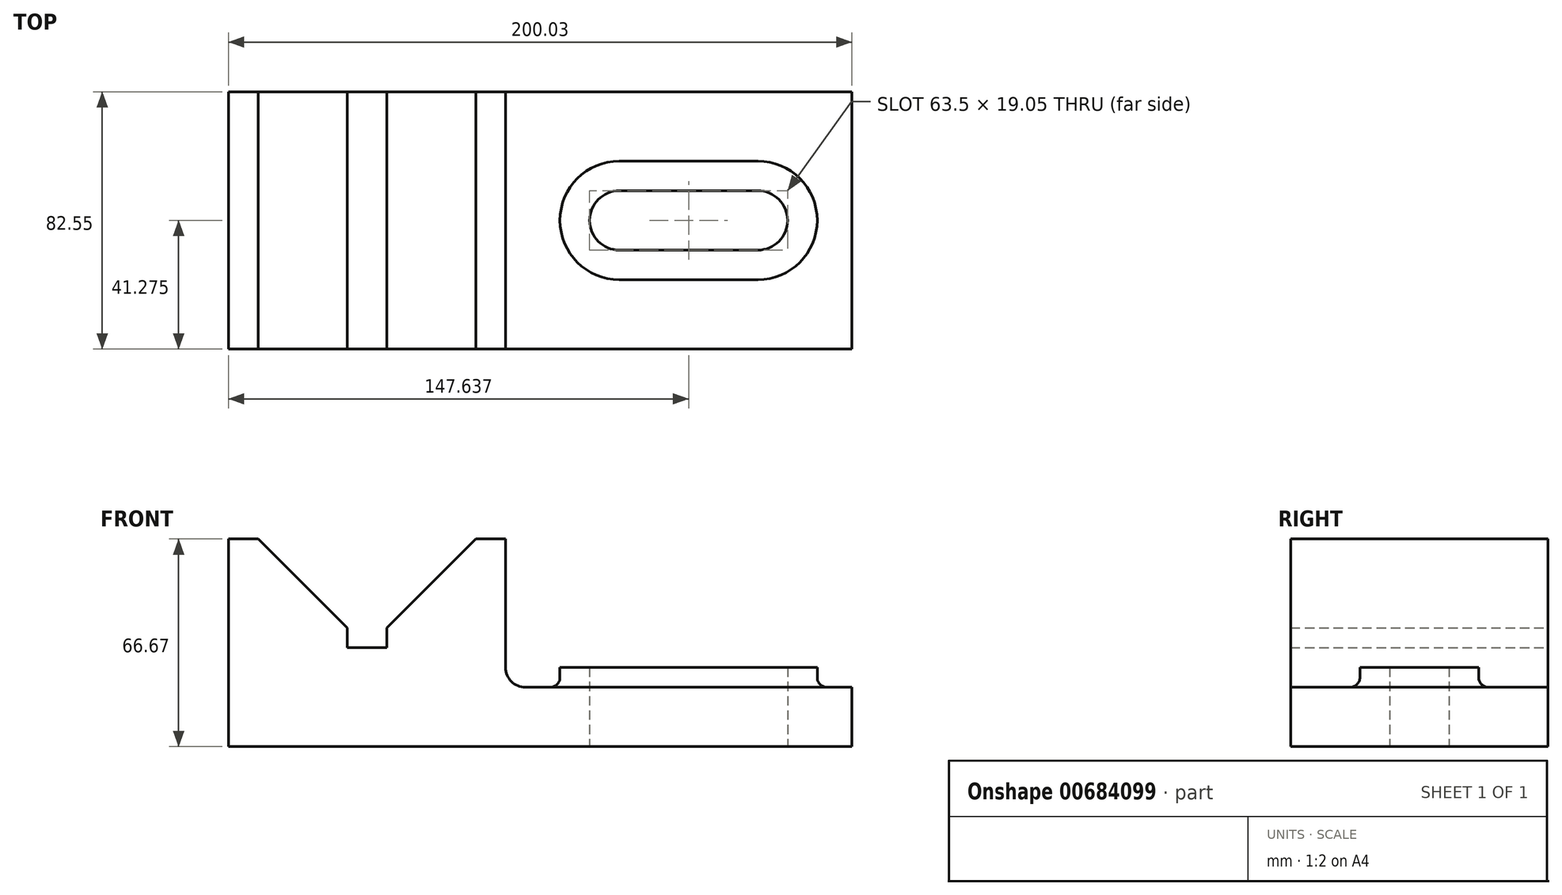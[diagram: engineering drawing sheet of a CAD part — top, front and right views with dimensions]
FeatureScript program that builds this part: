
annotation { "Feature Type Name" : "Feature", "Feature Type Description" : "" }
export const myFeature = defineFeature(function(context is Context, id is Id, definition is map)
    precondition{}
    {
        {
            var Q0;
            Q0=qCreatedBy(makeId("Front.planeOp"),FACE);
            var sketch = newSketch(context, id + "F0", { "sketchPlane" : qUnion([Q0])});
            skLineSegment(sketch, "E0", {"start": v(0, 0) * mm, "end": v(0, 66.68) * mm});
            skLineSegment(sketch, "E1", {"start": v(0, 0) * mm, "end": v(200.03, 0) * mm});
            skLineSegment(sketch, "E2", {"start": v(0, 66.68) * mm, "end": v(9.53, 66.68) * mm});
            skLineSegment(sketch, "E3", {"start": v(79.38, 66.68) * mm, "end": v(88.9, 66.68) * mm});
            skLineSegment(sketch, "E4", {"start": v(9.53, 66.68) * mm, "end": v(38.1, 38.1) * mm});
            skLineSegment(sketch, "E5", {"start": v(79.38, 66.68) * mm, "end": v(50.8, 38.1) * mm});
            skPoint(sketch, "E6", {"position": v(44.45, 31.75) * mm});
            skLineSegment(sketch, "E7", {"start": v(38.1, 38.1) * mm, "end": v(38.1, 31.75) * mm});
            skLineSegment(sketch, "E8", {"start": v(38.1, 31.75) * mm, "end": v(50.8, 31.75) * mm});
            skLineSegment(sketch, "E9", {"start": v(50.8, 31.75) * mm, "end": v(50.8, 38.1) * mm});
            skLineSegment(sketch, "E10", {"start": v(200.03, 0) * mm, "end": v(200.03, 19.05) * mm});
            skLineSegment(sketch, "E11", {"start": v(88.9, 26.67) * mm, "end": v(88.9, 26.26) * mm});
            skLineSegment(sketch, "E12", {"start": v(200.03, 19.05) * mm, "end": v(95.25, 19.05) * mm});
            skLineSegment(sketch, "E13", {"start": v(88.9, 66.68) * mm, "end": v(88.9, 25.4) * mm});
            skArc(sketch, "E14", {"start": v(88.9, 25.4) * mm, "mid": v(90.76, 20.9) * mm, "end": v(95.25, 19.05) * mm});
            skSolve(sketch);
        }
        {
            var Q0;
            Q0 = qSketchRegion(id + "F0", true);
            extrude(context, id + "F1", {"entities" : qUnion([Q0]), "depth" : 82.55 * mm, "offsetDistance" : 25.4 * mm});
        }
        {
            var Q0;
            Q0=makeQuery(id+"F1.opExtrude","SWEPT_FACE",FACE,{"disambiguationData":[OSD([sQuery(id+"F0.wireOp",EDGE,"E12")])]});
            var sketch = newSketch(context, id + "F2", { "sketchPlane" : qUnion([Q0])});
            skArc(sketch, "E15", {"start": v(125.41, -31.75) * mm, "mid": v(115.89, -41.28) * mm, "end": v(125.41, -50.8) * mm});
            skArc(sketch, "E16", {"start": v(125.41, -22.23) * mm, "mid": v(106.36, -41.28) * mm, "end": v(125.41, -60.33) * mm});
            skArc(sketch, "E17", {"start": v(169.86, -50.8) * mm, "mid": v(179.39, -41.28) * mm, "end": v(169.86, -31.75) * mm});
            skArc(sketch, "E18", {"start": v(169.86, -60.33) * mm, "mid": v(188.91, -41.28) * mm, "end": v(169.86, -22.23) * mm});
            skLineSegment(sketch, "E19", {"start": v(125.41, -60.33) * mm, "end": v(169.86, -60.33) * mm});
            skLineSegment(sketch, "E20", {"start": v(169.86, -22.23) * mm, "end": v(125.41, -22.23) * mm});
            skPoint(sketch, "E21.orphan", {"position": v(147.64, -41.28) * mm});
            skLineSegment(sketch, "E22", {"start": v(125.41, -50.8) * mm, "end": v(169.86, -50.8) * mm});
            skLineSegment(sketch, "E23", {"start": v(169.86, -31.75) * mm, "end": v(125.41, -31.75) * mm});
            skSolve(sketch);
        }
        {
            var Q0;
            Q0 = qSketchRegion(id + "F2", true);
            extrude(context, id + "F3", {"entities" : qUnion([Q0]), "operationType" : NewBodyOperationType.ADD, "depth" : 6.35 * mm, "offsetDistance" : 25.4 * mm});
        }
        {
            var Q0;
            Q0=makeQuery(id+"F2.imprint","IMPRINT",FACE,{"disambiguationData":[TD([[makeQuery(id+"F2.imprint","IMPRINT",EDGE,{"derivedFrom":sQuery(id+"F2.wireOp",EDGE,"E15")}),1.0]])]});
            extrude(context, id + "F4", {"entities" : qUnion([Q0]), "operationType" : NewBodyOperationType.REMOVE, "oppositeDirection" : true, "depth" : 25.4 * mm, "offsetDistance" : 25.4 * mm});
        }
        {
            var Q0;
            Q0=makeQuery(id+"F3.opExtrude","CAP_EDGE",EDGE,{"disambiguationData":[OSD([sQuery(id+"F2.wireOp",EDGE,"E18")])],"isStart":true});
            fillet(context, id + "F5", {"entities" : qUnion([Q0]), "radius" : 3.17 * mm, "tangentPropagation" : true, "allowEdgeOverflow" : false});
        }
    });
